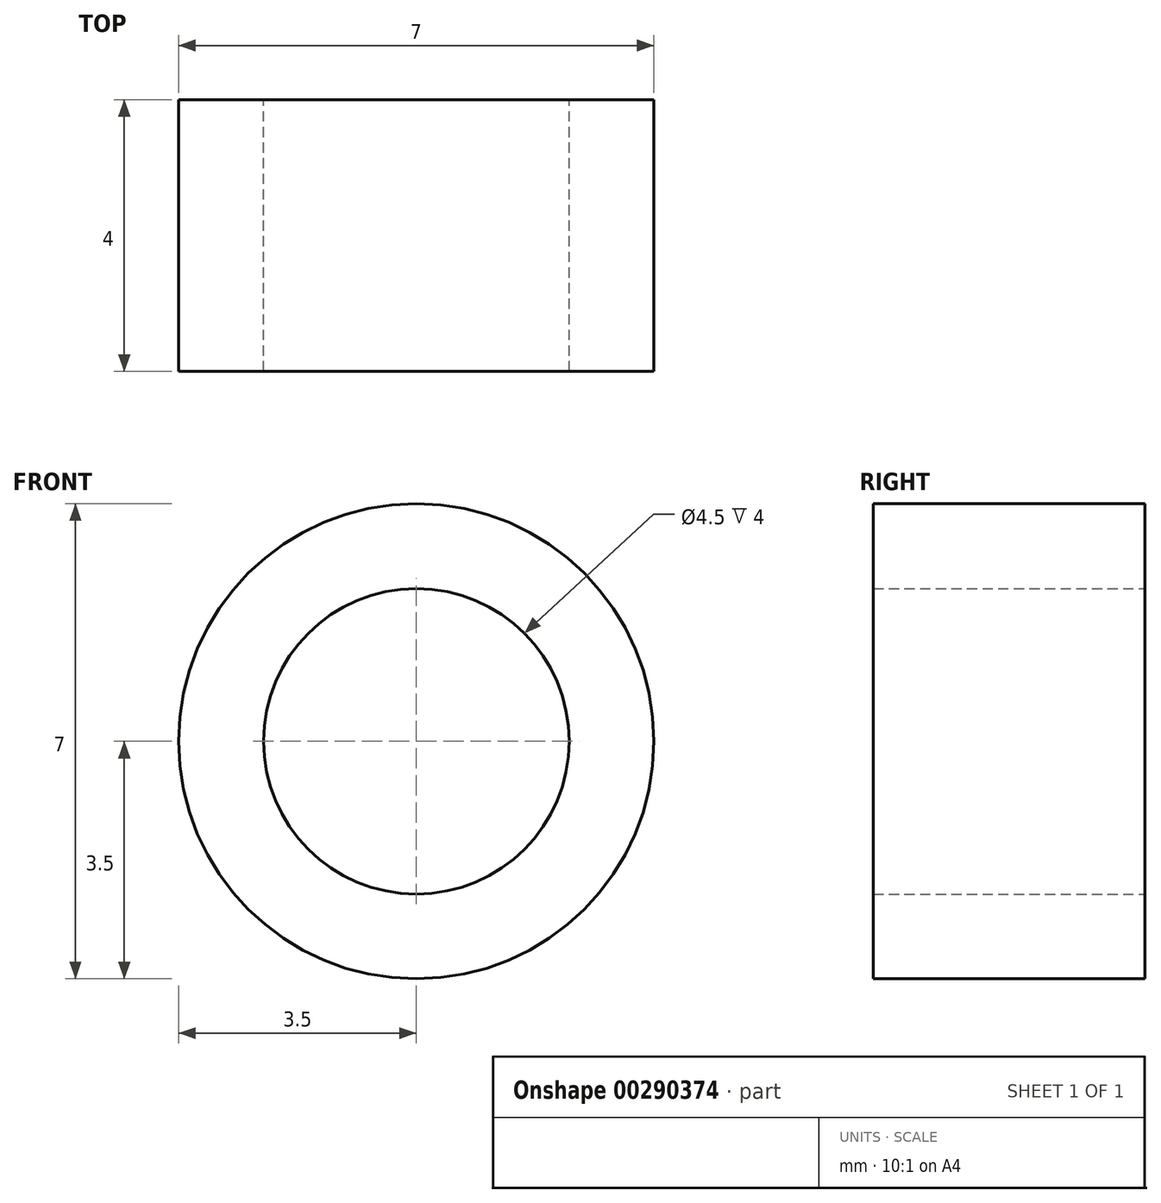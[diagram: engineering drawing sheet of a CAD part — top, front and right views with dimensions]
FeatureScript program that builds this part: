
annotation { "Feature Type Name" : "Feature", "Feature Type Description" : "" }
export const myFeature = defineFeature(function(context is Context, id is Id, definition is map)
    precondition{}
    {
        {
            var Q0;
            Q0=qCreatedBy(makeId("Front.planeOp"),FACE);
            var sketch = newSketch(context, id + "F0", { "sketchPlane" : qUnion([Q0])});
            skCircle(sketch, "E0", {"center": v(0, 0) * mm, "radius": 3.5 * mm});
            skSolve(sketch);
        }
        {
            var Q0;
            Q0=makeQuery(id+"F0.imprint","IMPRINT",FACE,{"disambiguationData":[TD([[makeQuery(id+"F0.imprint","IMPRINT",EDGE,{"derivedFrom":sQuery(id+"F0.wireOp",EDGE,"E0")}),1.0]])]});
            extrude(context, id + "F1", {"entities" : qUnion([Q0]), "depth" : 4 * mm});
        }
        {
            var Q0;
            Q0=qCreatedBy(makeId("Front.planeOp"),FACE);
            var sketch = newSketch(context, id + "F2", { "sketchPlane" : qUnion([Q0])});
            skCircle(sketch, "E1", {"center": v(0, 0) * mm, "radius": 2.25 * mm});
            skSolve(sketch);
        }
        {
            var Q0;
            Q0=makeQuery(id+"F2.imprint","IMPRINT",FACE,{"disambiguationData":[TD([[makeQuery(id+"F2.imprint","IMPRINT",EDGE,{"derivedFrom":sQuery(id+"F2.wireOp",EDGE,"E1")}),1.0]])]});
            extrude(context, id + "F3", {"entities" : qUnion([Q0]), "operationType" : NewBodyOperationType.REMOVE, "endBound" : BoundingType.THROUGH_ALL, "depth" : 25 * mm});
        }
    });
